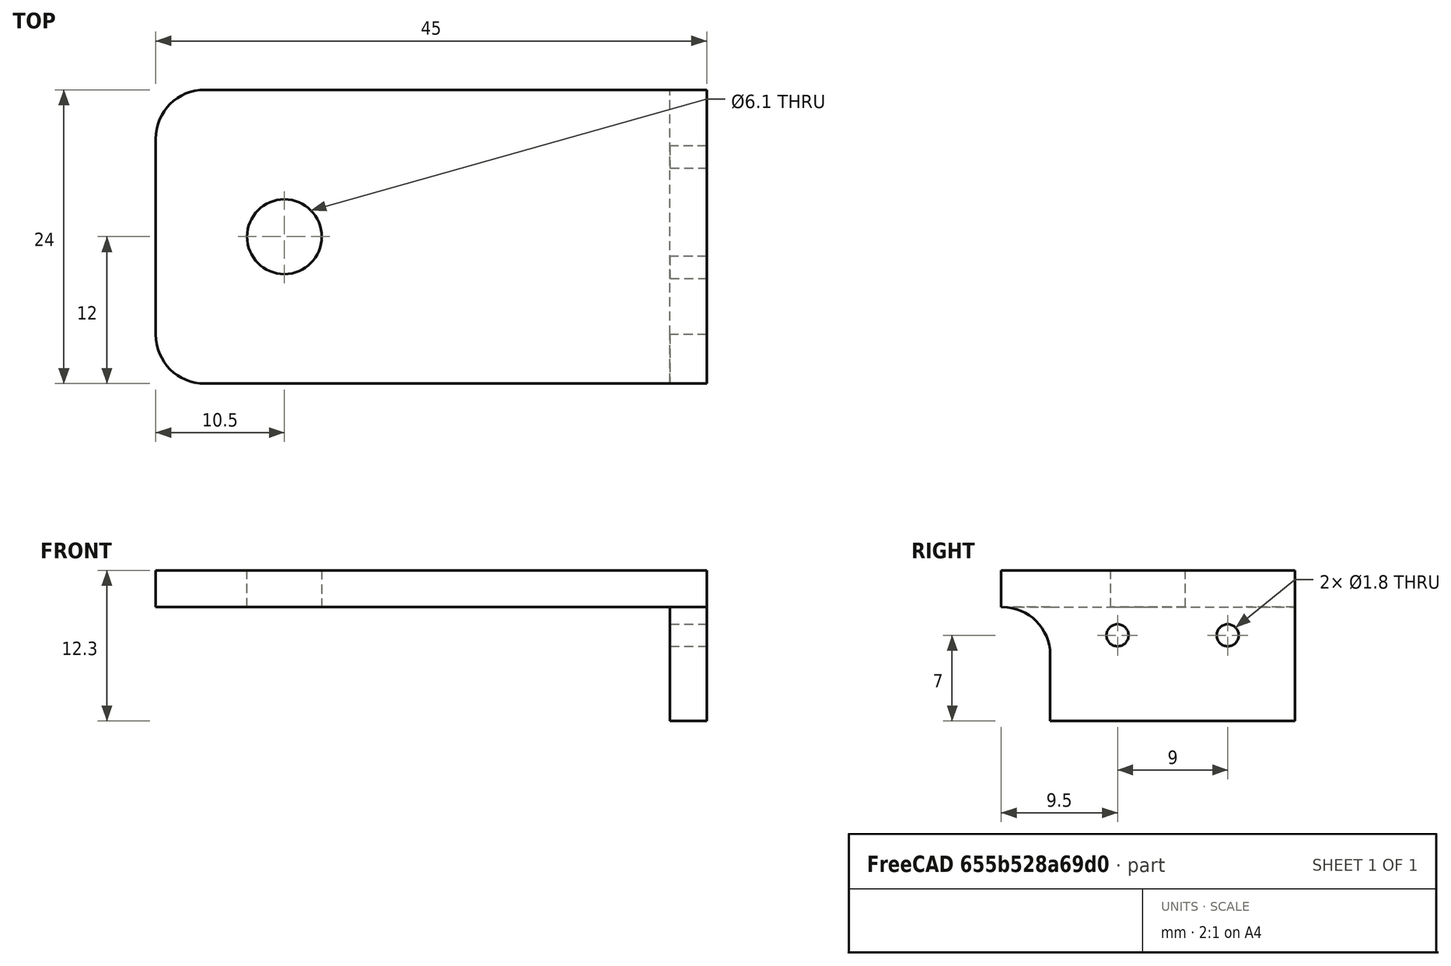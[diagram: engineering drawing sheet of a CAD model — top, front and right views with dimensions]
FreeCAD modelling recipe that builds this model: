
FCSTD DOCUMENT  (FreeCAD 0.21R33771 (Git))
Label: z_end_stop
License: All rights reserved
LicenseURL: https://en.wikipedia.org/wiki/All_rights_reserved
objects: Sketcher::SketchObject×4, PartDesign::Pad×2, PartDesign::Pocket×2, PartDesign::Fillet×2, PartDesign::Body×1, Mesh::Feature×1
note: 17 computed .brp shape members not serialized (recipe doc carries the construction recipe); baked Part::Feature solids carry a one-line shape summary decoded from their .brp

FEATURE [Sketcher::SketchObject] Sketch
  FullyConstrained = true
  MapMode = 5
  Support = -> [XY_Plane]
  sketch-geometry (4):
    g0: LineSegment StartX=0 StartY=12 StartZ=0 EndX=45 EndY=12 EndZ=0
    g1: LineSegment StartX=45 StartY=12 StartZ=0 EndX=45 EndY=-12 EndZ=0
    g2: LineSegment StartX=45 StartY=-12 StartZ=0 EndX=0 EndY=-12 EndZ=0
    g3: LineSegment StartX=0 StartY=-12 StartZ=0 EndX=0 EndY=12 EndZ=0
  constraints (11):
    c: Coincident(g0,g1)
    c: Coincident(g1,g2)
    c: Coincident(g2,g3)
    c: Coincident(g3,g0)
    c: Horizontal(g0)
    c: Horizontal(g2)
    c: Vertical(g1)
    c: DistanceX(g0,g0) = 45
    c: DistanceY(g1,g1) = 24
    c: Symmetric(g0,g2,g-1)
    c: PointOnObject(g0,g-2)
FEATURE [PartDesign::Pad] Pad
  Direction = (0,0,1)
  Length = 3
  Length2 = 10
  Profile = -> Sketch
  ReferenceAxis = -> Sketch [N_Axis]
  Type = 0
FEATURE [Sketcher::SketchObject] Sketch001
  ExternalGeometry = -> [Pad]
  FullyConstrained = true
  MapMode = 5
  Placement = pos=(0,0,3) rot=(0,0,1;0rad)
  Support = -> [Pad]
  sketch-geometry (1):
    g0: Circle CenterX=10.5 CenterY=0 CenterZ=0 NormalX=0 NormalY=0 NormalZ=1 AngleXU=0 Radius=3.05
  constraints (3):
    c: PointOnObject(g0,g-1)
    c: Diameter(g0) = 6.1
    c: DistanceX(g0,g-3) = 34.5
FEATURE [PartDesign::Pocket] Pocket
  BaseFeature = -> Pad
  Direction = (0,0,-1)
  Length = 5
  Length2 = 5
  Profile = -> Sketch001
  ReferenceAxis = -> Sketch001 [N_Axis]
  Type = 1
FEATURE [Sketcher::SketchObject] Sketch002
  ExternalGeometry = -> [Pocket]
  FullyConstrained = true
  MapMode = 5
  Placement = pos=(0,0,0) rot=(1,0,0;3.14159rad)
  Support = -> [Pocket]
  sketch-geometry (4):
    g0: LineSegment StartX=45 StartY=8 StartZ=0 EndX=42 EndY=8 EndZ=0
    g1: LineSegment StartX=42 StartY=8 StartZ=0 EndX=42 EndY=-12 EndZ=0
    g2: LineSegment StartX=42 StartY=-12 StartZ=0 EndX=45 EndY=-12 EndZ=0
    g3: LineSegment StartX=45 StartY=-12 StartZ=0 EndX=45 EndY=8 EndZ=0
  constraints (11):
    c: Coincident(g0,g1)
    c: Coincident(g1,g2)
    c: Coincident(g2,g3)
    c: Coincident(g3,g0)
    c: Horizontal(g0)
    c: Horizontal(g2)
    c: Vertical(g1)
    c: Vertical(g3)
    c: Coincident(g2,g-3)
    c: DistanceX(g0,g0) = 3
    c: DistanceY(g1,g1) = 20
FEATURE [PartDesign::Pad] Pad001
  BaseFeature = -> Pocket
  Direction = (0,0,-1)
  Length = 9.3
  Length2 = 10
  Profile = -> Sketch002
  ReferenceAxis = -> Sketch002 [N_Axis]
  Type = 0
FEATURE [Sketcher::SketchObject] Sketch003
  ExternalGeometry = -> [Pad001]
  FullyConstrained = true
  MapMode = 5
  Placement = pos=(45,0,0) rot=(0.57735,0.57735,0.57735;2.0944rad)
  Support = -> [Pad001]
  sketch-geometry (2):
    g0: Circle CenterX=6.5 CenterY=-2.3 CenterZ=0 NormalX=0 NormalY=0 NormalZ=1 AngleXU=0 Radius=0.9
    g1: Circle CenterX=-2.5 CenterY=-2.3 CenterZ=0 NormalX=0 NormalY=0 NormalZ=1 AngleXU=0 Radius=0.9
  constraints (6):
    c: Equal(g1,g0)
    c: Diameter(g1) = 1.8
    c: Horizontal(g1,g0)
    c: DistanceY(g-3,g0) = 7
    c: DistanceX(g1,g0) = 9
    c: DistanceX(g0,g-3) = 5.5
FEATURE [PartDesign::Pocket] Pocket001
  BaseFeature = -> Pad001
  Direction = (-1,0,0)
  Length = 5
  Length2 = 5
  Profile = -> Sketch003
  ReferenceAxis = -> Sketch003 [N_Axis]
  Type = 1
FEATURE [PartDesign::Fillet] Fillet
  Base = -> Pocket001 [Edge14]
  BaseFeature = -> Pocket001
  Radius = 3.9
  SupportTransform = false
  UseAllEdges = false
FEATURE [PartDesign::Fillet] Fillet001
  Base = -> Fillet [Edge20,Edge25]
  BaseFeature = -> Fillet
  Radius = 4
  SupportTransform = false
  UseAllEdges = false
FEATURE [PartDesign::Body] Body
  Group = -> [Sketch,Pad,Sketch001,Pocket,Sketch002,Pad001,Sketch003,Pocket001,Fillet,Fillet001]
  Origin = -> Origin
  Tip = -> Fillet001
FEATURE [Mesh::Feature] Mesh  label="Fillet001 (Meshed)"
